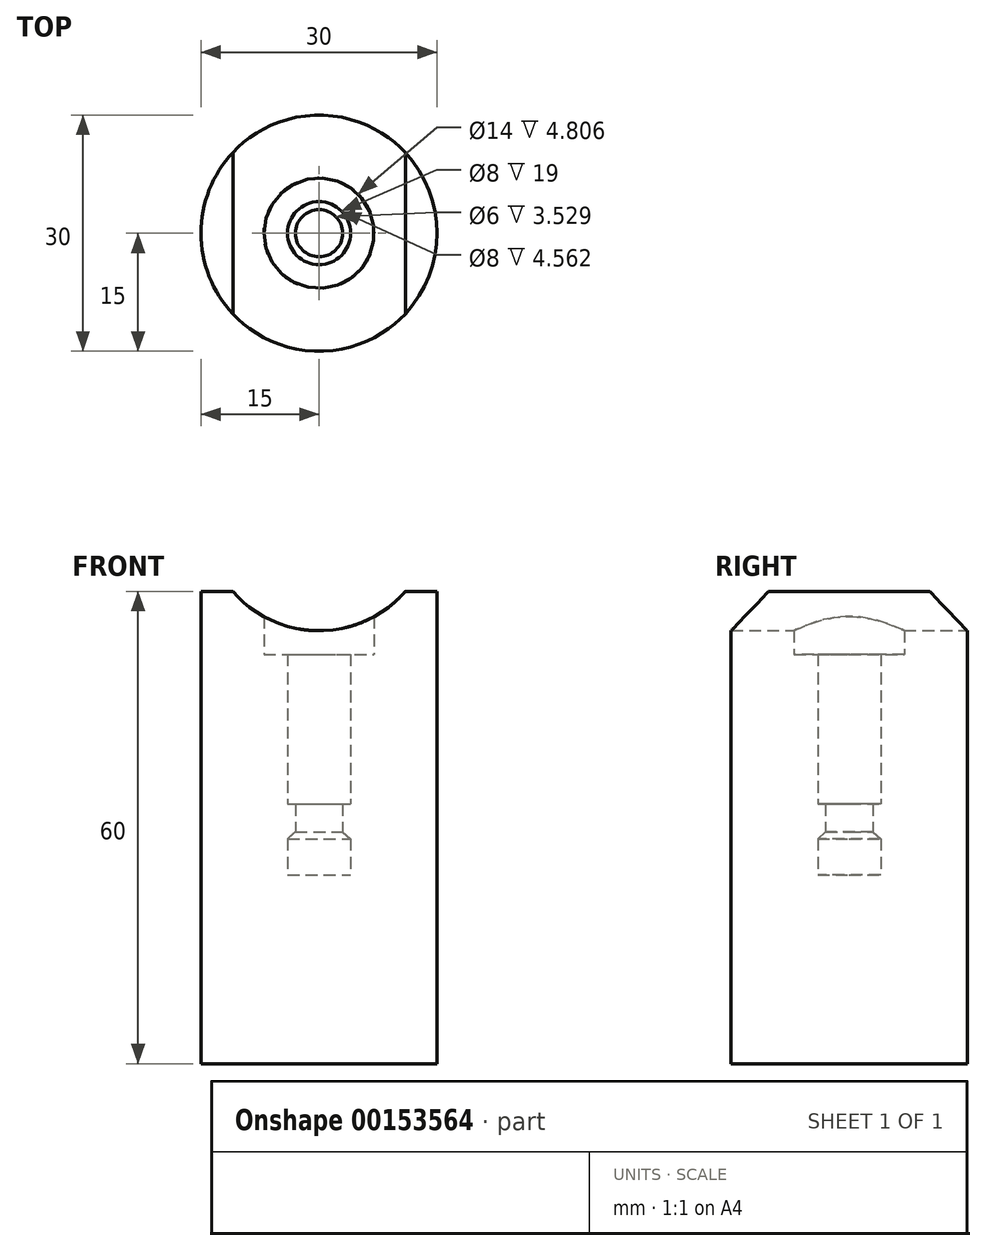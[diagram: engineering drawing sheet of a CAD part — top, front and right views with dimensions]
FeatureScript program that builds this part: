
annotation { "Feature Type Name" : "Feature", "Feature Type Description" : "" }
export const myFeature = defineFeature(function(context is Context, id is Id, definition is map)
    precondition{}
    {
        {
            var Q0;
            Q0=qCreatedBy(makeId("Front.planeOp"),FACE);
            var sketch = newSketch(context, id + "F0", { "sketchPlane" : qUnion([Q0])});
            skLineSegment(sketch, "E0", {"start": v(4, 27) * mm, "end": v(4, 8) * mm});
            skLineSegment(sketch, "E1", {"start": v(4, 0) * mm, "end": v(4, 3.56) * mm});
            skLineSegment(sketch, "E2", {"start": v(4, 8) * mm, "end": v(3, 8) * mm});
            skLineSegment(sketch, "E3", {"start": v(3, 8) * mm, "end": v(3, 4.47) * mm});
            skLineSegment(sketch, "E4.trimOffspring", {"start": v(4, 3.56) * mm, "end": v(4, 0) * mm});
            skLineSegment(sketch, "E5", {"start": v(4, 27) * mm, "end": v(7, 27) * mm});
            skLineSegment(sketch, "E6", {"start": v(7, 27) * mm, "end": v(7, 30) * mm});
            skLineSegment(sketch, "E7", {"start": v(7, 30) * mm, "end": v(15, 30) * mm});
            skLineSegment(sketch, "E8", {"start": v(15, 30) * mm, "end": v(15, 27) * mm});
            skLineSegment(sketch, "E9", {"start": v(15, 27) * mm, "end": v(15, -25) * mm});
            skLineSegment(sketch, "E10", {"start": v(15, -25) * mm, "end": v(0, -25) * mm});
            skLineSegment(sketch, "E11", {"start": v(0, -25) * mm, "end": v(0, 0) * mm});
            skLineSegment(sketch, "E12", {"start": v(0, -1) * mm, "end": v(4, -1) * mm});
            skLineSegment(sketch, "E13", {"start": v(4, -1) * mm, "end": v(4, 0) * mm});
            skLineSegment(sketch, "E14", {"start": v(3, 4.47) * mm, "end": v(4, 3.56) * mm});
            skSolve(sketch);
        }
        {
            var Q0;
            Q0=makeQuery(id+"F0.imprint","IMPRINT",FACE,{"disambiguationData":[TD([[makeQuery(id+"F0.imprint","IMPRINT",EDGE,{"derivedFrom":sQuery(id+"F0.wireOp",EDGE,"E0")}),1.0]])]});
            var Q1;
            Q1=sQuery(id+"F0.wireOp",EDGE,"E11");
            revolve(context, id + "F1", {"entities" : qUnion([Q0]), "axis" : qUnion([Q1]), "revolveType" : RevolveType.FULL});
        }
        {
            var Q0;
            Q0=makeQuery(id+"F1.opRevolve","SWEPT_FACE",FACE,{"disambiguationData":[OSD([sQuery(id+"F0.wireOp",EDGE,"E7")])]});
            extrude(context, id + "F2", {"entities" : qUnion([Q0]), "operationType" : NewBodyOperationType.ADD, "depth" : 5 * mm});
        }
        {
            var Q0;
            Q0=qCreatedBy(makeId("Front.planeOp"),FACE);
            var sketch = newSketch(context, id + "F3", { "sketchPlane" : qUnion([Q0])});
            skPoint(sketch, "E15.center.orphan", {"position": v(0, 45.52) * mm});
            skArc(sketch, "E16", {"start": v(-11, 35.05) * mm, "mid": v(0, 30) * mm, "end": v(11, 35.05) * mm});
            skLineSegment(sketch, "E17", {"start": v(11, 35.05) * mm, "end": v(-11, 35.05) * mm});
            skSolve(sketch);
        }
        {
            var Q0;
            Q0 = qSketchRegion(id + "F3", true);
            extrude(context, id + "F4", {"entities" : qUnion([Q0]), "operationType" : NewBodyOperationType.REMOVE, "endBound" : BoundingType.SYMMETRIC, "depth" : 40 * mm});
        }
    });
